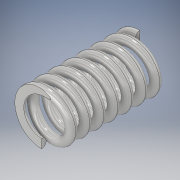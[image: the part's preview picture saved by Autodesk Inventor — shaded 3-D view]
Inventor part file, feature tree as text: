
AUTODESK INVENTOR PART (.ipt)
format: ipt  version: 2017 (Build 210142000, 142)  size: 493,568 bytes
history: native  units: in
note: dims shown in document units (in); Inventor stores cm internally (conversion verified against a paired STEP export)
features: sketch x3, extrude x2, helix x1, plane x1
ambient origin geometry x8: Origin, YZ Plane, XZ Plane, XY Plane, X Axis, Y Axis, Z Axis, Center Point
bodies: Solid1 (feature_tree)
feature tree (7):
  helix  "Coil1"  [1 undecoded]
  extrude  "Extrusion1"  Depth=0.4331in TaperAngle=0.0deg
  plane  "Work Plane1"
  extrude  "Extrusion2"  Depth=0.4331in TaperAngle=0.0deg
  sketch  "Sketch1"  dims[d3=0.2362in]
  sketch  "Sketch2"  dims[d4=0.3937in d5=0.4331in d6=2.6575in d7=0.0in d8=90.0deg d9=45.0deg d10=90.0deg d11=45.0deg d12=0.3937in d13=0.0in]
  sketch  "Sketch4"  dims[d14=0.4331in d15=0.3937in d16=0.0in]
note: 1 required parameter value undecoded (feature->parameter linkage not recoverable at this tier; creation-order binding heuristic only, values carry confidence <= 0.55)
